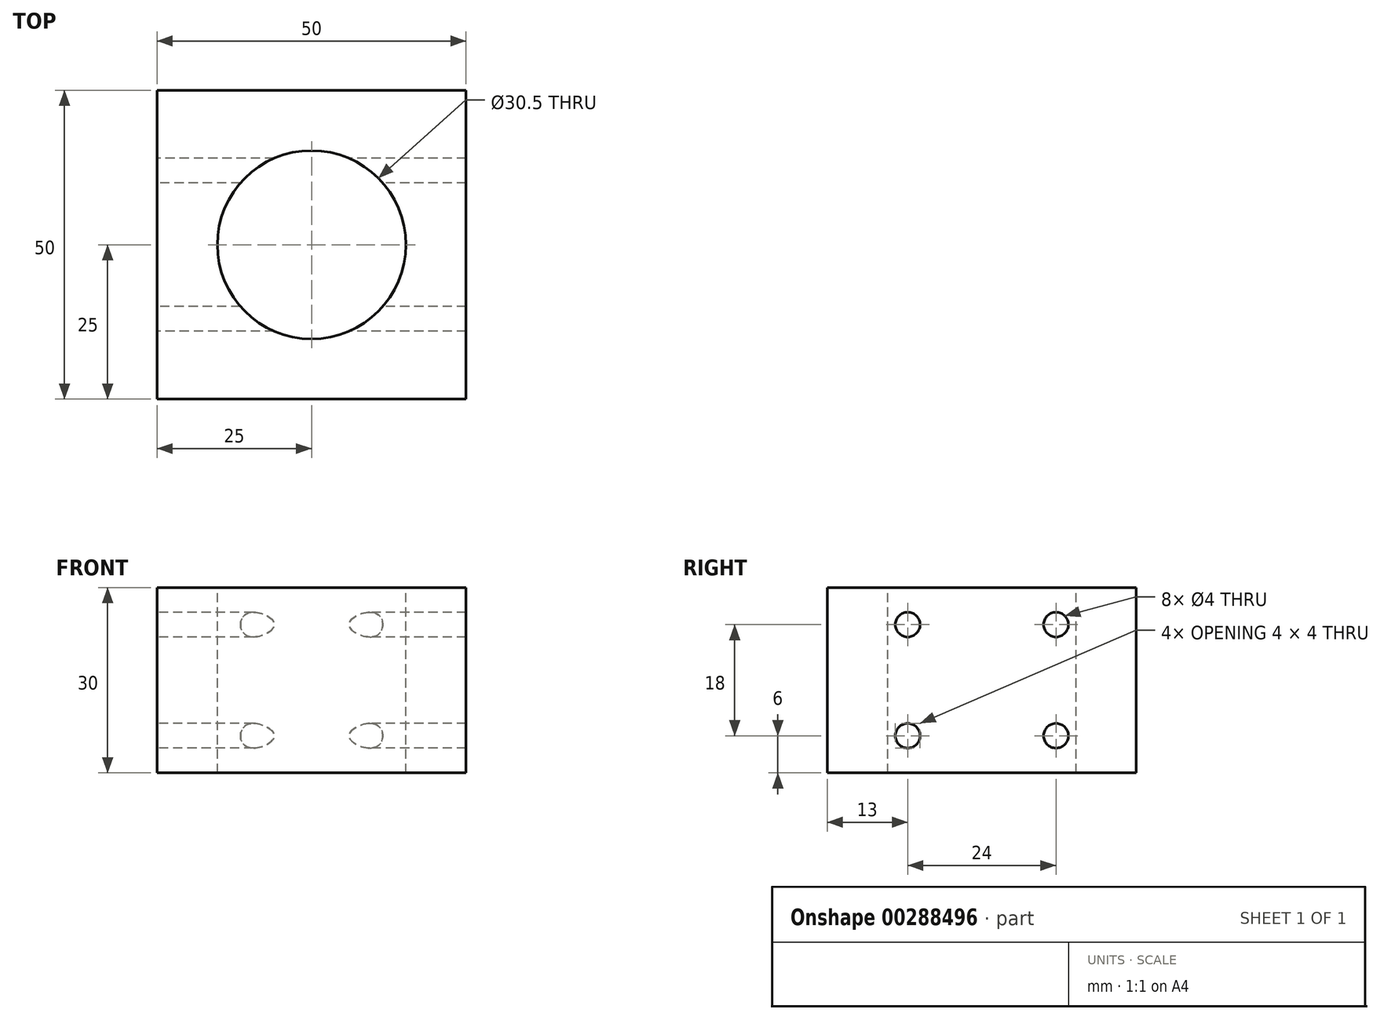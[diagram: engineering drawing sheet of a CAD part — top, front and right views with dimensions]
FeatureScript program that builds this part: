
annotation { "Feature Type Name" : "Feature", "Feature Type Description" : "" }
export const myFeature = defineFeature(function(context is Context, id is Id, definition is map)
    precondition{}
    {
        {
            var Q0;
            Q0=qCreatedBy(makeId("Right.planeOp"),FACE);
            var sketch = newSketch(context, id + "F0", { "sketchPlane" : qUnion([Q0])});
            skLineSegment(sketch, "E0.bottom", {"start": v(25, -15) * mm, "end": v(-25, -15) * mm});
            skLineSegment(sketch, "E0.top", {"start": v(25, 15) * mm, "end": v(-25, 15) * mm});
            skLineSegment(sketch, "E0.left", {"start": v(25, -15) * mm, "end": v(25, 15) * mm});
            skLineSegment(sketch, "E0.right", {"start": v(-25, -15) * mm, "end": v(-25, 15) * mm});
            skPoint(sketch, "E0.middle", {"position": v(0, 0) * mm});
            skCircle(sketch, "E1", {"center": v(-12, -9) * mm, "radius": 2 * mm});
            skPoint(sketch, "E2.middle", {"position": v(0, 15) * mm});
            skPoint(sketch, "E3.startSnap0", {"position": v(0, -15) * mm});
            skPoint(sketch, "E4.startSnap0", {"position": v(-25, 0) * mm});
            skCircle(sketch, "E5", {"center": v(-12, 9) * mm, "radius": 2 * mm});
            skLineSegment(sketch, "E6", {"start": v(0, 30.13) * mm, "end": v(0, -23.26) * mm, "construction": true});
            skCircle(sketch, "E7.MirrorC", {"center": v(12, 9) * mm, "radius": 2 * mm});
            skCircle(sketch, "E8.MirrorC", {"center": v(12, -9) * mm, "radius": 2 * mm});
            skSolve(sketch);
        }
        {
            var Q0;
            Q0=makeQuery(id+"F0.imprint","IMPRINT",FACE,{"disambiguationData":[TD([[makeQuery(id+"F0.imprint","IMPRINT",EDGE,{"derivedFrom":sQuery(id+"F0.wireOp",EDGE,"E0.bottom")}),-1.0]])]});
            var Q1;
            {var subQ5=sQuery(id+"F0.wireOp",EDGE,"E2.bottom");Q1=makeQuery(id+"F0.imprint","IMPRINT",FACE,{"disambiguationData":[TD([[makeQuery(id+"F0.imprint","IMPRINT",EDGE,{"derivedFrom":subQ5}),-1.0]])]});}
            extrude(context, id + "F1", {"entities" : qUnion([Q0, Q1]), "endBound" : BoundingType.SYMMETRIC, "depth" : 50 * mm});
        }
        {
            var Q0;
            Q0=makeQuery(id+"F1.opExtrude","SWEPT_FACE",FACE,{"disambiguationData":[OSD([sQuery(id+"F0.wireOp",EDGE,"E0.top")])]});
            var sketch = newSketch(context, id + "F2", { "sketchPlane" : qUnion([Q0])});
            skCircle(sketch, "E9", {"center": v(0, 0) * mm, "radius": 15.25 * mm});
            skSolve(sketch);
        }
        {
            var Q0;
            Q0 = qSketchRegion(id + "F2", true);
            extrude(context, id + "F3", {"entities" : qUnion([Q0]), "operationType" : NewBodyOperationType.REMOVE, "endBound" : BoundingType.THROUGH_ALL, "oppositeDirection" : true, "depth" : 18 * mm});
        }
    });
